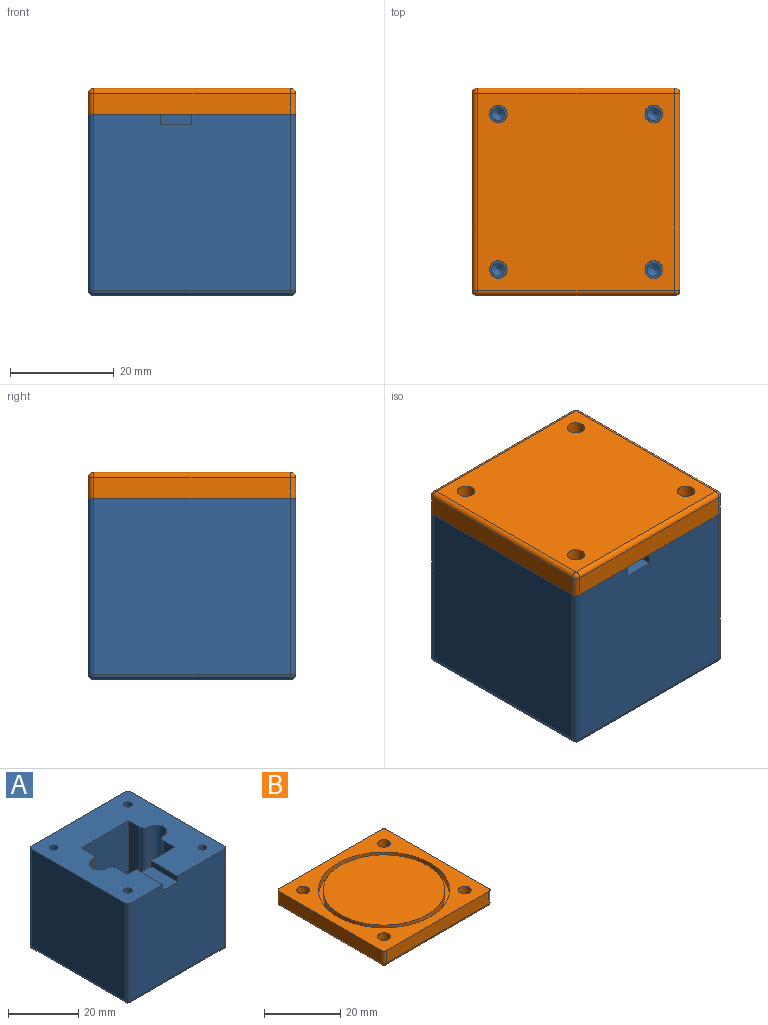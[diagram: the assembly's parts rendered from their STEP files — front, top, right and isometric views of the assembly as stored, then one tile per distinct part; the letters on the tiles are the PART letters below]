
ASSEMBLY  parts=2 mates=1
PART A: 45 faces, bbox 40x40x35 mm
  f0: plane 40x40mm, normal (0,0,1), area 1110mm2, adj f1,f7,f8,f9,f10,f11,f12,f13
  f1: plane 30x19mm, normal (0,1,0), area 558mm2, adj f0,f6,f14,f15,f30,f31,f32
  f2: cylinder r=6.25mm len=12.5mm, axis (0,0,-1), area 39.3mm2, adj f3,f4
  f3: plane 15x15mm, normal (0,0,1), area 54mm2, adj f2,f5
  f4: plane 38x38mm, normal (0,0,-1), area 1321.3mm2, adj f2,f36,f37,f41,f42
  f5: cylinder r=7.5mm len=15mm, axis (0,0,-1), area 188.5mm2, adj f3,f6
  f6: plane 28.77x18.5mm, normal (0,0,1), area 228.3mm2, adj f1,f5,f7,f8,f9,f10,f11,f12
  f7: plane 30x19mm, normal (0,-1,0), area 570mm2, adj f0,f6,f10,f11
  f8: cylinder r=3mm len=30mm, axis (0,0,-1), area 295.2mm2, adj f0,f6,f12,f13
  f9: cylinder r=3mm len=30mm, axis (0,0,-1), area 295.2mm2, adj f0,f6,f16,f21
  f10: plane 30x4.54mm, normal (1,0,0), area 136.2mm2, adj f0,f6,f7,f21
  f11: plane 30x4.54mm, normal (-1,0,0), area 136.2mm2, adj f0,f6,f7,f12
  f12: cylinder r=1.78mm len=30mm, axis (0,0,-1), area 79mm2, adj f0,f6,f8,f11
  f13: cylinder r=1.78mm len=30mm, axis (0,0,-1), area 79mm2, adj f0,f6,f8,f14
  f14: plane 30x4.54mm, normal (-1,0,0), area 136.2mm2, adj f0,f1,f6,f13
  f15: plane 30x4.54mm, normal (1,0,0), area 136.2mm2, adj f0,f1,f6,f16
  f16: cylinder r=1.78mm len=30mm, axis (0,0,-1), area 79mm2, adj f0,f6,f9,f15
  f17: plane 38x34mm, normal (0,1,0), area 1292mm2, adj f0,f38,f42,f44
  f18: plane 38x34mm, normal (-1,0,0), area 1292mm2, adj f0,f35,f41,f44
  f19: plane 38x34mm, normal (0,-1,0), area 1280mm2, adj f0,f30,f31,f32,f33,f35,f36
  f20: plane 38x34mm, normal (1,0,0), area 1292mm2, adj f0,f33,f37,f38
  f21: cylinder r=1.78mm len=30mm, axis (0,0,-1), area 79mm2, adj f0,f6,f9,f10
  f22: cone r=0mm half-angle=59deg, axis (0,0,1), area 5.7mm2, adj f23
  f23: cylinder r=1.25mm len=16.5mm, axis (0,0,1), area 129.6mm2, adj f0,f22
  f24: cone r=0mm half-angle=59deg, axis (0,0,1), area 5.7mm2, adj f25
  f25: cylinder r=1.25mm len=16.5mm, axis (0,0,1), area 129.6mm2, adj f0,f24
  f26: cone r=0mm half-angle=59deg, axis (0,0,1), area 5.7mm2, adj f27
  f27: cylinder r=1.25mm len=16.5mm, axis (0,0,1), area 129.6mm2, adj f0,f26
  f28: cone r=0mm half-angle=59deg, axis (0,0,1), area 5.7mm2, adj f29
  f29: cylinder r=1.25mm len=16.5mm, axis (0,0,1), area 129.6mm2, adj f0,f28
  f30: plane 10.75x2mm, normal (-1,0,0), area 21.5mm2, adj f0,f1,f19,f32
  f31: plane 10.75x2mm, normal (1,0,0), area 21.5mm2, adj f0,f1,f19,f32
  f32: plane 10.75x6mm, normal (0,0,1), area 64.5mm2, adj f1,f19,f30,f31
  f33: cylinder r=1mm len=34mm, axis (0,0,1), area 53.4mm2, adj f0,f19,f20,f34
  f34: sphere r=1mm, area 1.6mm2, adj f33,f36,f37
  f35: cylinder r=1mm len=34mm, axis (0,0,-1), area 53.4mm2, adj f0,f18,f19,f39
  f36: cylinder r=1mm len=38mm, axis (1,0,0), area 59.7mm2, adj f4,f19,f34,f39
  f37: cylinder r=1mm len=38mm, axis (0,1,0), area 59.7mm2, adj f4,f20,f34,f40
  f38: cylinder r=1mm len=34mm, axis (0,0,-1), area 53.4mm2, adj f0,f17,f20,f40
  f39: sphere r=1mm, area 1.6mm2, adj f35,f36,f41
  f40: sphere r=1mm, area 1.6mm2, adj f37,f38,f42
  f41: cylinder r=1mm len=38mm, axis (0,-1,0), area 59.7mm2, adj f4,f18,f39,f43
  f42: cylinder r=1mm len=38mm, axis (-1,0,0), area 59.7mm2, adj f4,f17,f40,f43
  f43: sphere r=1mm, area 1.6mm2, adj f41,f42,f44
  f44: cylinder r=1mm len=34mm, axis (0,0,1), area 53.4mm2, adj f0,f17,f18,f43
PART B: 26 faces, bbox 40x40x5 mm
  f0: plane 38x4mm, normal (0,1,0), area 152mm2, adj f4,f19,f23,f25
  f1: plane 38x4mm, normal (-1,0,0), area 152mm2, adj f4,f16,f22,f25
  f2: plane 38x4mm, normal (0,-1,0), area 152mm2, adj f4,f14,f16,f17
  f3: plane 38x4mm, normal (1,0,0), area 152mm2, adj f4,f14,f18,f19
  f4: plane 40x40mm, normal (0,0,1), area 628mm2, adj f0,f1,f2,f3,f7,f10,f11,f12
  f5: plane 38x38mm, normal (0,0,-1), area 1407.7mm2, adj f10,f11,f12,f13,f17,f18,f22,f23
  f6: cylinder r=16mm len=32mm, axis (0,0,1), area 201.1mm2, adj f8,f9
  f7: cylinder r=17.25mm len=34.5mm, axis (0,0,1), area 216.8mm2, adj f4,f8
  f8: plane 34.5x34.5mm, normal (0,0,1), area 130.6mm2, adj f6,f7
  f9: plane 32x32mm, normal (0,0,1), area 804.2mm2, adj f6
  f10: cylinder r=1.7mm len=5mm, axis (0,0,1), area 53.4mm2, adj f4,f5
  f11: cylinder r=1.7mm len=5mm, axis (0,0,1), area 53.4mm2, adj f4,f5
  f12: cylinder r=1.7mm len=5mm, axis (0,0,1), area 53.4mm2, adj f4,f5
  f13: cylinder r=1.7mm len=5mm, axis (0,0,1), area 53.4mm2, adj f4,f5
  f14: cylinder r=1mm len=4mm, axis (0,0,1), area 6.3mm2, adj f2,f3,f4,f15
  f15: sphere r=1mm, area 1.6mm2, adj f14,f17,f18
  f16: cylinder r=1mm len=4mm, axis (0,0,-1), area 6.3mm2, adj f1,f2,f4,f20
  f17: cylinder r=1mm len=38mm, axis (1,0,0), area 59.7mm2, adj f2,f5,f15,f20
  f18: cylinder r=1mm len=38mm, axis (0,1,0), area 59.7mm2, adj f3,f5,f15,f21
  f19: cylinder r=1mm len=4mm, axis (0,0,-1), area 6.3mm2, adj f0,f3,f4,f21
  f20: sphere r=1mm, area 1.6mm2, adj f16,f17,f22
  f21: sphere r=1mm, area 1.6mm2, adj f18,f19,f23
  f22: cylinder r=1mm len=38mm, axis (0,-1,0), area 59.7mm2, adj f1,f5,f20,f24
  f23: cylinder r=1mm len=38mm, axis (-1,0,0), area 59.7mm2, adj f0,f5,f21,f24
  f24: sphere r=1mm, area 1.6mm2, adj f22,f23,f25
  f25: cylinder r=1mm len=4mm, axis (0,0,1), area 6.3mm2, adj f0,f1,f4,f24
PLACE A t=(-17.86,-10.75,14.81)mm
PLACE B rot(axis=(0,1,0),180deg) t=(11.64,0,54.81)mm
MATE fastened A.f24 <-> B.f13  axis (0,0,1) through (6.64,-35,49.81)mm
